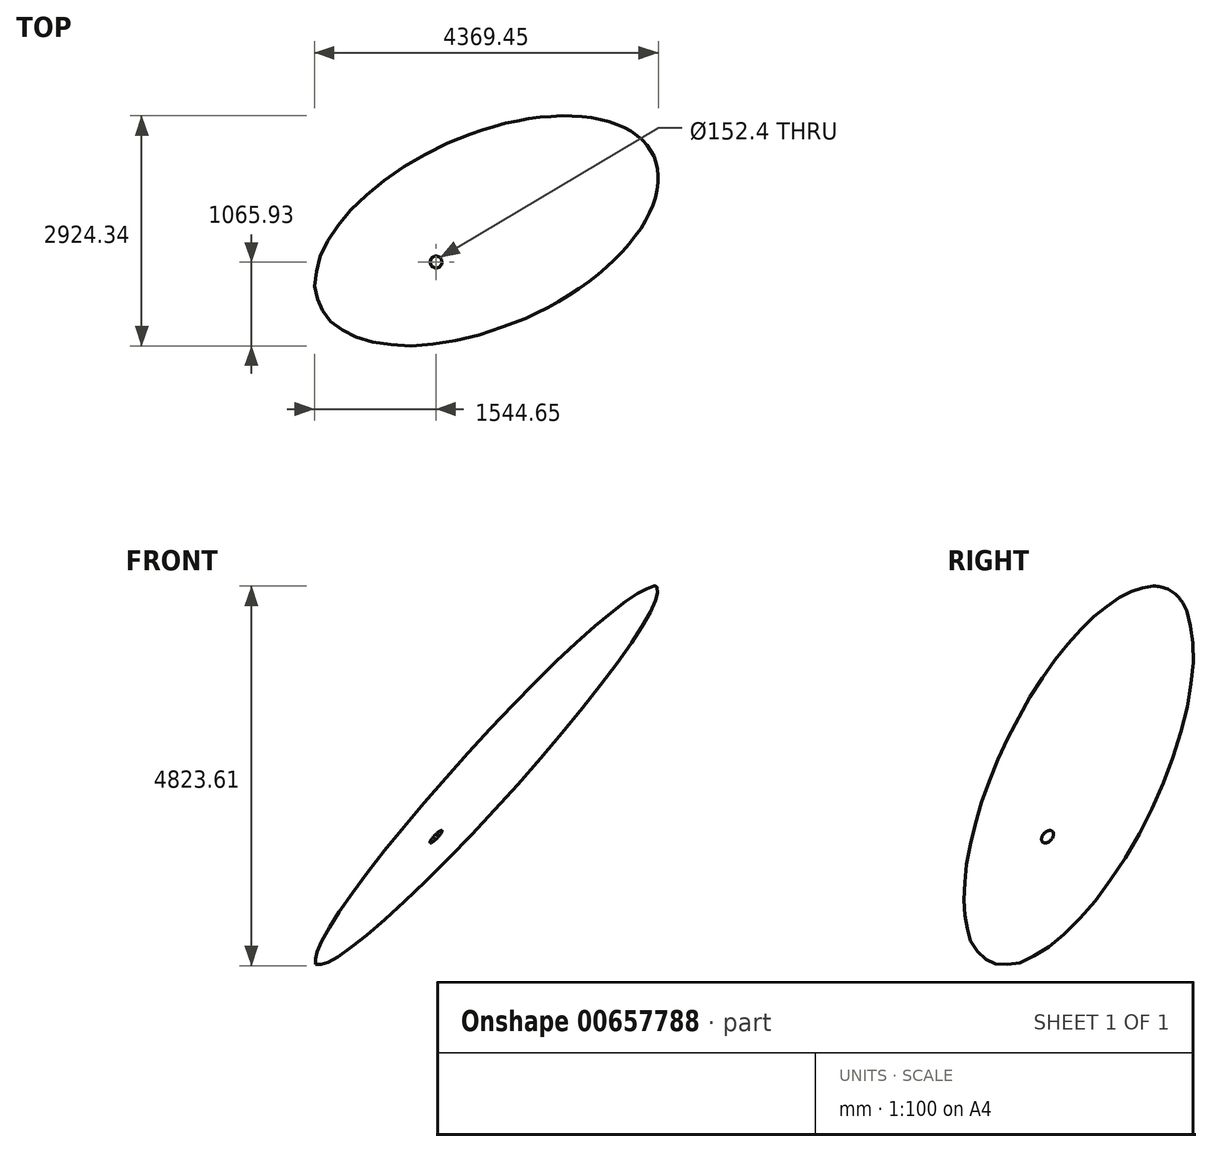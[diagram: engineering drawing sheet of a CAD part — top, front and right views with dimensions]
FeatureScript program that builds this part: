
annotation { "Feature Type Name" : "Feature", "Feature Type Description" : "" }
export const myFeature = defineFeature(function(context is Context, id is Id, definition is map)
    precondition{}
    {
        {
            assignVariable(context, id + "F0", {"name" : "Azimuth", "anyValue" : 156});
        }
        {
            assignVariable(context, id + "F1", {"name" : "Dip", "anyValue" : 46});
        }
        {
            assignVariable(context, id + "F2", {"name" : "Width", "anyValue" : 0.02});
        }
        {
            var Q0;
            Q0=qCreatedBy(makeId("Top.planeOp"),FACE);
            var sketch = newSketch(context, id + "F3", { "sketchPlane" : qUnion([Q0])});
            skEllipse(sketch, "E0", {"center": v(0, 0) * mm, "majorRadius": 1219.2 * mm, "minorRadius": 3352.8 * mm, "majorAxis": v(0, 1)});
            skLineSegment(sketch, "E1", {"start": v(0, 1965.96) * mm, "end": v(0, -1965.96) * mm, "construction": true});
            skLineSegment(sketch, "E2", {"start": v(-2819.4, 0) * mm, "end": v(2819.4, 0) * mm, "construction": true});
            skLineSegment(sketch, "E3.0", {"start": v(640.08, 1219.2) * mm, "end": v(640.08, -1219.2) * mm, "construction": true});
            skLineSegment(sketch, "E4.0", {"start": v(-3352.8, -396.24) * mm, "end": v(3352.8, -396.24) * mm, "construction": true});
            skSolve(sketch);
        }
        {
            var Q0;
            Q0=qCreatedBy(makeId("Top.planeOp"),FACE);
            var sketch = newSketch(context, id + "F4", { "sketchPlane" : qUnion([Q0])});
            skLineSegment(sketch, "E5", {"start": v(0, 0) * mm, "end": v(640.08, 0) * mm});
            skLineSegment(sketch, "E6", {"start": v(640.08, 0) * mm, "end": v(640.08, -396.24) * mm});
            skSolve(sketch);
        }
        {
            var Q0;
            Q0=qSketchRegion(id+"F3",true);
            extrude(context, id + "F5", {"entities" : qUnion([Q0]), "depth" : (getVariable(context, 'Width')) * mm});
        }
        {
            var Q0;
            Q0=qCreatedBy(makeId("Front.planeOp"),FACE);
            var sketch = newSketch(context, id + "F6", { "sketchPlane" : qUnion([Q0])});
            skLineSegment(sketch, "E7", {"start": v(0, 0) * mm, "end": v(0, -3627.12) * mm, "construction": true});
            skSolve(sketch);
        }
        {
            var Q0;
            Q0=makeQuery(id+"F5.opExtrude","SWEPT_BODY",BODY,{"disambiguationData":[OSD([sQuery(id+"F3.wireOp",EDGE,"E0"),sQuery(id+"F3.wireOp",EDGE,"TMMzbr5i-4nV4-ZnMr-aG6B-IGJ66UyS6uPJ")])]});
            var Q1;
            Q1=sQuery(id+"F3.wireOp",EDGE,"E1");
            transform(context, id + "F7", {"entities" : qUnion([Q0]), "transformType" : TransformType.ROTATION, "transformAxis" : qUnion([Q1]), "angle" : (getVariable(context, 'Dip')) * degree, "oppositeDirection" : true, "makeCopy" : false});
        }
        {
            var Q0;
            Q0=makeQuery(id+"F5.opExtrude","SWEPT_BODY",BODY,{"disambiguationData":[OSD([sQuery(id+"F3.wireOp",EDGE,"E0")])]});
            var Q1;
            Q1=sQuery(id+"F6.wireOp",EDGE,"E7");
            transform(context, id + "F8", {"entities" : qUnion([Q0]), "transformType" : TransformType.ROTATION, "transformAxis" : qUnion([Q1]), "angle" : (getVariable(context, 'Azimuth')) * degree, "makeCopy" : false});
        }
        {
            var Q0;
            Q0=makeQuery(id+"F5.opExtrude","SWEPT_BODY",BODY,{"disambiguationData":[OSD([sQuery(id+"F3.wireOp",EDGE,"E0"),sQuery(id+"F3.wireOp",EDGE,"TMMzbr5i-4nV4-ZnMr-aG6B-IGJ66UyS6uPJ")])]});
            var Q1;
            Q1=sQuery(id+"F4.wireOp",EDGE,"E5");
            transform(context, id + "F9", {"entities" : qUnion([Q0]), "transformType" : TransformType.TRANSLATION_ENTITY, "oppositeDirectionEntity" : false, "transformLine" : qUnion([Q1]), "makeCopy" : false});
        }
        {
            var Q0;
            Q0=makeQuery(id+"F5.opExtrude","SWEPT_BODY",BODY,{"disambiguationData":[OSD([sQuery(id+"F3.wireOp",EDGE,"E0"),sQuery(id+"F3.wireOp",EDGE,"TMMzbr5i-4nV4-ZnMr-aG6B-IGJ66UyS6uPJ")])]});
            var Q1;
            Q1=sQuery(id+"F4.wireOp",EDGE,"E6");
            transform(context, id + "F10", {"entities" : qUnion([Q0]), "transformType" : TransformType.TRANSLATION_ENTITY, "oppositeDirectionEntity" : true, "transformLine" : qUnion([Q1]), "makeCopy" : false});
        }
        {
            var Q0;
            Q0=qCreatedBy(makeId("Top.planeOp"),FACE);
            var sketch = newSketch(context, id + "F11", { "sketchPlane" : qUnion([Q0])});
            skCircle(sketch, "E8", {"center": v(0, 0) * mm, "radius": 76.2 * mm});
            skSolve(sketch);
        }
        {
            var Q0;
            Q0=qSketchRegion(id+"F11",true);
            extrude(context, id + "F12", {"entities" : qUnion([Q0]), "operationType" : NewBodyOperationType.REMOVE, "endBound" : BoundingType.THROUGH_ALL, "oppositeDirection" : true, "depth" : 30.48 * mm, "hasSecondDirection" : true, "secondDirectionBound" : SecondDirectionBoundingType.THROUGH_ALL, "secondDirectionOppositeDirection" : false, "secondDirectionDepth" : 30.48 * mm});
        }
        {
            var Q0;
            Q0=makeQuery(id+"F5.opExtrude","SWEPT_BODY",BODY,{"disambiguationData":[OSD([sQuery(id+"F3.wireOp",EDGE,"E0")])]});
            var Q1;
            Q1=sQuery(id+"F6.wireOp",EDGE,"E7");
            transform(context, id + "F13", {"entities" : qUnion([Q0]), "transformType" : TransformType.TRANSLATION_ENTITY, "oppositeDirectionEntity" : false, "transformLine" : qUnion([Q1]), "makeCopy" : false});
        }
    });
